# Revit family: Domotics-DomesticRanges-GEWISS-CHORUS_DATA-SOCKET-OUTLET_TV-SAT
name_source: partatom
category: Apparecchi elettrici
revit_build: Autodesk Revit 2016 (Build: 20161004_0715(x64)
units: mm (PartAtom-declared; Revit-internal decimal feet)

## family parameters
Condiviso = Sì
Host = Superficie
Mantenere orientamento annotazione = Sì
Punto di calcolo locali = Sì
Quota connettore circolare = Usa diametro
Taglio con vuoti quando caricato = Sì
Tipo di parte = Normale

## types (12) — shared parameters
Carico apparente = 0 VA
Catalogue = DOMOTICS
Catalogue Range = CHORUS - DOMESTIC RANGE
Electrocod = 0131
IDF = a22b526e-bee1-44ee-8d36-1e99666e472c
IDT = bacfc3d2-aa9f-48c9-8e08-3d3563ba30a4
Immagine tipo = GW14371.jpg
N. poli = 1
Produttore = GEWISS S.p.A.
Prospetto di default = 1219 mm
Technical sheet = https://www.gewiss.com
Tipo_ = SYSTEM PRESE TV-SAT_GENERICO : GW titanio
URL = https://www.gewiss.com
Version file RFA = 19.0
Volt = 230 V

## per-type parameters (varying)
| type | Descrizione | EAN code | Modello |
| GW10373 - TV/SAT SOCKET 1M THROUGH 10dB F.CONN F W | TV/SAT SOCKET 1M THROUGH 10dB F.CONN F W | 8011564259379 | GW10373 |
| GW14373 - TV/SAT SOCKET 1M THROUGH 10dB F.CONN F T | TV/SAT SOCKET 1M THROUGH 10dB F.CONN F T | 8011564267022 | GW14373 |
| GW12374 - TV/SAT SOCKET 1M THROUGH 14dB F.CONN F B | TV/SAT SOCKET 1M THROUGH 14dB F.CONN F B | 8011564268982 | GW12374 |
| GW12371 - TV/SAT SOCKET 1M DIRECT F.CONN FEM B | TV/SAT SOCKET 1M DIRECT F.CONN FEM B | 8011564266674 | GW12371 |
| GW10372 - TV/SAT SOCKET 1M THROUGH 5dB F.CONN F W | TV/SAT SOCKET 1M THROUGH 5dB F.CONN F W | 8011564259362 | GW10372 |
| GW10374 - TV/SAT SOCKET 1M THROUGH 14dB F.CONN F W | TV/SAT SOCKET 1M THROUGH 14dB F.CONN F W | 8011564259386 | GW10374 |
| GW14372 - TV/SAT SOCKET 1M THROUGH 5dB F.CONN F T | TV/SAT SOCKET 1M THROUGH 5dB F.CONN F T | 8011564267015 | GW14372 |
| GW12372 - TV/SAT SOCKET 1M THROUGH 5dB F.CONN F B | TV/SAT SOCKET 1M THROUGH 5dB F.CONN F B | 8011564268968 | GW12372 |
| GW14374 - TV/SAT SOCKET 1M THROUGH 14dB F.CONN F T | TV/SAT SOCKET 1M THROUGH 14dB F.CONN F T | 8011564267039 | GW14374 |
| GW12373 - TV/SAT SOCKET 1M THROUGH 10dB F.CONN F B | TV/SAT SOCKET 1M THROUGH 10dB F.CONN F B | 8011564268975 | GW12373 |
| GW14371 - TV/SAT SOCKET 1M DIRECT F.CONN FEM. T | TV/SAT SOCKET 1M DIRECT F.CONN FEM. T | 8011564266803 | GW14371 |
| GW10371 - TV/SAT SOCKET 1M DIRECT F.CONN F WHITE | TV/SAT SOCKET 1M DIRECT F.CONN F WHITE | 8011564258976 | GW10371 |

## geometry (parser evidence)
native form markers: Sweep x2
no freeform markers — native parametric forms only
